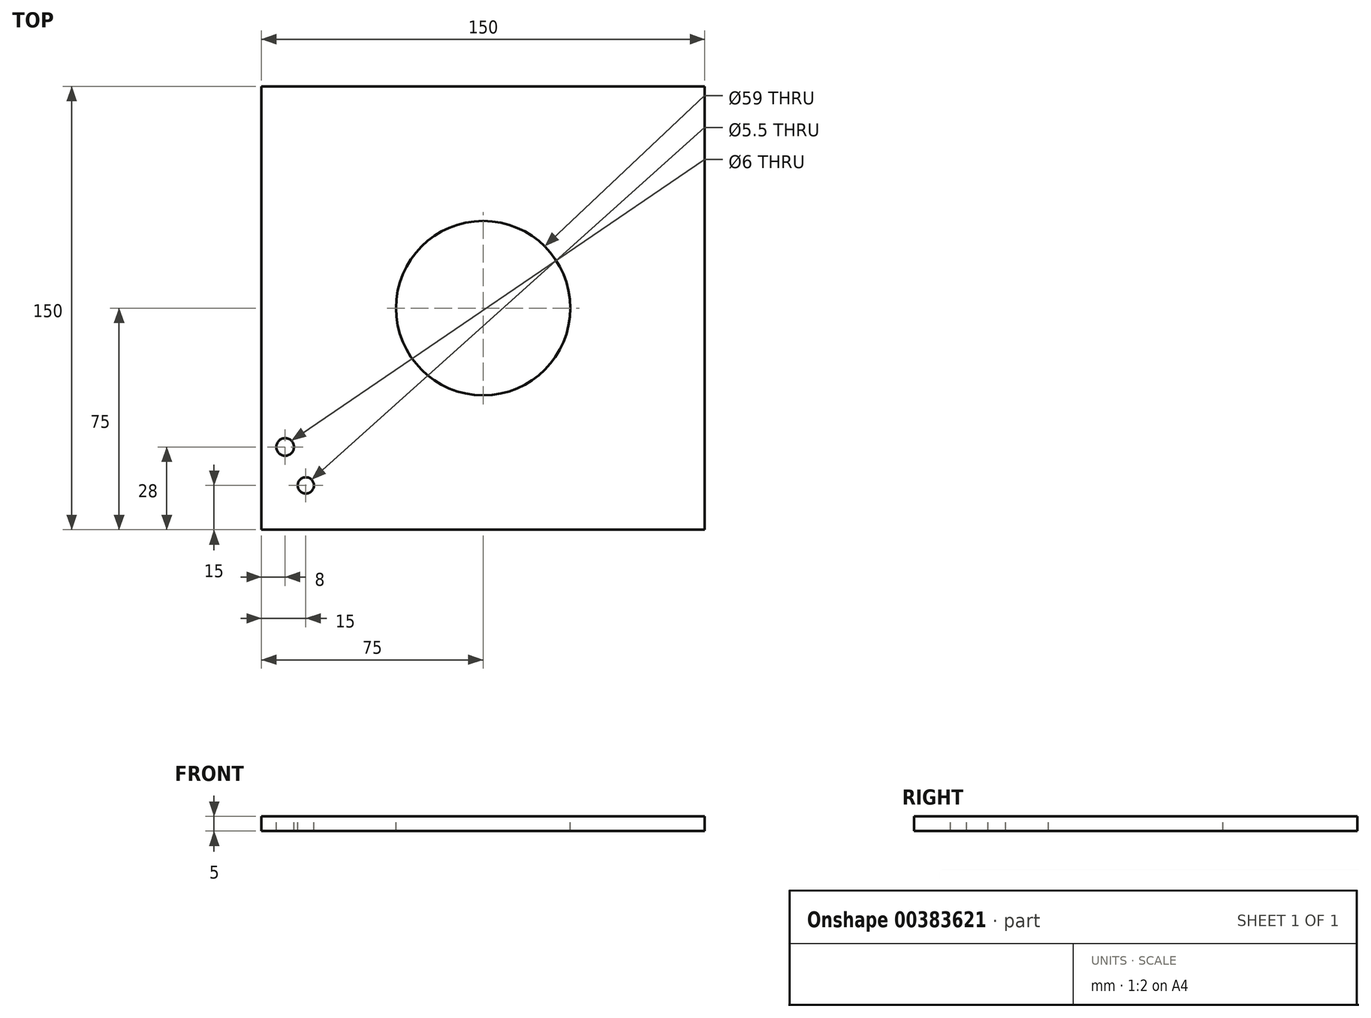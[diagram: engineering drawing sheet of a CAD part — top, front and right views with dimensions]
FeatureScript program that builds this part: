
annotation { "Feature Type Name" : "Feature", "Feature Type Description" : "" }
export const myFeature = defineFeature(function(context is Context, id is Id, definition is map)
    precondition{}
    {
        {
            var Q0;
            Q0=qCreatedBy(makeId("Top.planeOp"),FACE);
            var sketch = newSketch(context, id + "F0", { "sketchPlane" : qUnion([Q0])});
            skLineSegment(sketch, "E0", {"start": v(-177.56, -50) * mm, "end": v(188.12, -50) * mm});
            skCircle(sketch, "E1", {"center": v(0, 0) * mm, "radius": 24 * mm});
            skSolve(sketch);
        }
        {
            var Q0;
            Q0=qCreatedBy(makeId("Top.planeOp"),FACE);
            var sketch = newSketch(context, id + "F1", { "sketchPlane" : qUnion([Q0])});
            skCircle(sketch, "E2", {"center": v(-19.25, -5.43) * mm, "radius": 4 * mm});
            skCircle(sketch, "E3", {"center": v(-19.25, -5.43) * mm, "radius": 9.5 * mm, "construction": true});
            skSolve(sketch);
        }
        {
            var Q0;
            Q0=qCreatedBy(makeId("Top.planeOp"),FACE);
            var sketch = newSketch(context, id + "F2", { "sketchPlane" : qUnion([Q0])});
            skLineSegment(sketch, "E4.bottom", {"start": v(-75, 75) * mm, "end": v(75, 75) * mm});
            skLineSegment(sketch, "E4.top", {"start": v(-75, -75) * mm, "end": v(75, -75) * mm});
            skLineSegment(sketch, "E4.left", {"start": v(-75, 75) * mm, "end": v(-75, -75) * mm});
            skLineSegment(sketch, "E4.right", {"start": v(75, 75) * mm, "end": v(75, -75) * mm});
            skCircle(sketch, "E5", {"center": v(0, 0) * mm, "radius": 29.5 * mm});
            skSolve(sketch);
        }
        {
            var Q0;
            Q0=makeQuery(id+"F2.imprint","IMPRINT",FACE,{"disambiguationData":[TD([[makeQuery(id+"F2.imprint","IMPRINT",EDGE,{"derivedFrom":sQuery(id+"F2.wireOp",EDGE,"LgkgOG5l-oDy4-2v9K-BSEM-c5lva1so4qZ2.bottom")}),1.0]])]});
            var Q1;
            Q1=makeQuery(id+"F2.imprint","IMPRINT",FACE,{"disambiguationData":[TD([[makeQuery(id+"F2.imprint","IMPRINT",EDGE,{"derivedFrom":sQuery(id+"F2.wireOp",EDGE,"E4.bottom")}),-1.0]])]});
            extrude(context, id + "F3", {"entities" : qUnion([Q0, Q1]), "oppositeDirection" : true, "depth" : 5 * mm});
        }
        {
            var Q0;
            Q0=qCreatedBy(makeId("Top.planeOp"),FACE);
            var sketch = newSketch(context, id + "F4", { "sketchPlane" : qUnion([Q0])});
            skPoint(sketch, "E6", {"position": v(-60, -60) * mm});
            skSolve(sketch);
        }
        {
            var Q0;
            Q0=sQuery(id+"F4.wireOp",VERTEX,"E6");
            var Q1;
            Q1=makeQuery(id+"F3.opExtrude","SWEPT_BODY",BODY,{"disambiguationData":[OSD([sQuery(id+"F2.wireOp",EDGE,"LgkgOG5l-oDy4-2v9K-BSEM-c5lva1so4qZ2.bottom"),sQuery(id+"F2.wireOp",EDGE,"LgkgOG5l-oDy4-2v9K-BSEM-c5lva1so4qZ2.top"),sQuery(id+"F2.wireOp",EDGE,"sBxC89SE-gP1B-1wLF-RGwt-KoprnWfLY1li"),sQuery(id+"F2.wireOp",EDGE,"RoB1l2Wv-41i7-Al06-1ras-OJaeqRDDCEy1"),sQuery(id+"F2.wireOp",EDGE,"E4.bottom"),sQuery(id+"F2.wireOp",EDGE,"E4.top"),sQuery(id+"F2.wireOp",EDGE,"E4.left"),sQuery(id+"F2.wireOp",EDGE,"E4.right")])]});
            hole(context, id + "F5", {"style" : HoleStyle.SIMPLE, "endStyle" : HoleEndStyle.THROUGH, "standardTappedOrClearance" : lookupTablePath({ "standard" : "ISO", "fit" : "Normal", "size" : "M5", "type" : "Clearance" }), "standardBlindInLast" : lookupTablePath({ "fit" : "Standard", "standard" : "ISO", "size" : "M5", "type" : "Clearance" }), "holeDiameter" : 5.5 * mm, "isTappedThrough" : true, "tappedDepth" : 12 * mm, "tapClearance" : 3, "locations" : qUnion([Q0]), "scope" : qUnion([Q1])});
        }
        {
            var Q0;
            Q0=qCreatedBy(makeId("Top.planeOp"),FACE);
            var sketch = newSketch(context, id + "F6", { "sketchPlane" : qUnion([Q0])});
            skCircle(sketch, "E7", {"center": v(-67, -47) * mm, "radius": 3 * mm});
            skSolve(sketch);
        }
        {
            var Q0;
            Q0=makeQuery(id+"F6.imprint","IMPRINT",FACE,{"disambiguationData":[TD([[makeQuery(id+"F6.imprint","IMPRINT",EDGE,{"derivedFrom":sQuery(id+"F6.wireOp",EDGE,"E7")}),1.0]])]});
            extrude(context, id + "F7", {"entities" : qUnion([Q0]), "operationType" : NewBodyOperationType.REMOVE, "endBound" : BoundingType.THROUGH_ALL, "oppositeDirection" : true, "depth" : 25 * mm});
        }
    });
